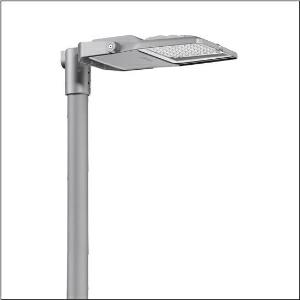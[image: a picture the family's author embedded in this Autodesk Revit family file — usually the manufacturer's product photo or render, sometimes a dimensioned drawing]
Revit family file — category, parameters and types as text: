
# Revit family: floodlight_fl_21_iq_mini___pl43_5xa7772c2a3a_c494
name_source: partatom
category: Lighting Fixtures
units: mm (PartAtom-declared; Revit-internal decimal feet)

## family parameters
Cut with Voids When Loaded = No
Host = Face
Light Source = No
Part Type = Normal
Room Calculation Point = No
Round Connector Dimension = Use Diameter
Shared = No

## types (1)
- --- (1 x LED, 12520 lm, 87.2 W, 3000K)
    Apparent Load = 87 VA
    CIE Flux Codes = 27 78 99 100 100
    Color Rendering = 70
    Color Temperature = 3000K
    Default Elevation = 1800 mm
    Description = Floodlight FL 21 iQ mini, floodlight, primary light control with lens, of PMMA, primary optical cover: protective disc, of toughened safety glass, transparent, light distribution: PL43, light emission: direct distribution, installation type: surface-mounted, LED, High Power LED, rated luminous flux: 12.520lm, luminous efficacy: 144lm/W, light colour: 730, colour temperature: 3000K, control: Auto-Match, Temp-Guard, Night-Set, Smart-Wire, Desk-Remote (wireless, voltage-free reading and setting of iQ features in the workshop via application-optimized NFC function/RFID function), optimised constant luminous flux control (CLO 2.0), Light-Fading, Lumen-Switch, with terminal, 6-pole, mains connection: 220..240V, AC, 50/60Hz, start of lifetime: 87W, end of service life: 92W, reduction: 40W, luminaire housing, of diecast aluminium, powder-coated, Siteco® metallic grey (DB 702S), corrosivity category C5 mid according to DIN EN ISO 12944, sealing non-destructively replaceable, please order mast flange separately, mast bracket, of steel, galvanised, powder-coated, protection rating (complete): IP66, insulation class (complete): insulation class II (safety insulation), certification: CE, ENEC, VDE, protection symbol: D, impact resistance: IK08, permissible operating ambient temperature: -40..+40°C, permissible operating ambient temperature for outdoor applications: -40..+50°C, standard: DIN EN 12944, LABS conformity tested according to VDMA 24364:2018-05, packaging unit: 1 piece

Light Distribution: PL43
    Height = 70 mm
    Lamp = 1 x LED
    Lamp Light Flux = 12520 lm
    Lamp Power = 87.2 W
    Lamp count = 1
    Length = 485 mm
    Luminous efficacy = 144 lm/W
    Manufacturer = Siteco
    ModVariant = No
    Model = 5XA7772C2A3A
    Number of Poles = 1
    OnlyDefault = Yes
    Power Factor = 1
    Product Name = Floodlight FL 21 iQ mini | PL43
    Product group = floodlight | pylon annexe
    ProductGroupID = 6200
    Protection Class = Protection class II
    Protection Degree = IP 66
    RLX_Detail_Level = 1
    RLX_Emergency_Light_Flux = 0 lm
    RLX_Emergency_Type = 0
    RLX_Emergency_Type_DB = No
    RlxData = <blob elided: 101189 chars, md5=20438680>
    Socket = socket
    Standby Power = 0 W
    System Light Flux = 12520 lm
    System Power = 87 W
    Type Comments = factory setting: luminous flux: 100 % | dim-lin: 254 | 456 mA
    Type Image = l_1007125.jpg
    URL = http://relux.com
    VarID = @adj_132639
    Voltage = 0 V
    Weight = 0.00 kg
    Width = 337 mm

## geometry (parser evidence)
native form markers: Blend x4, Sweep x11
no freeform markers — native parametric forms only
